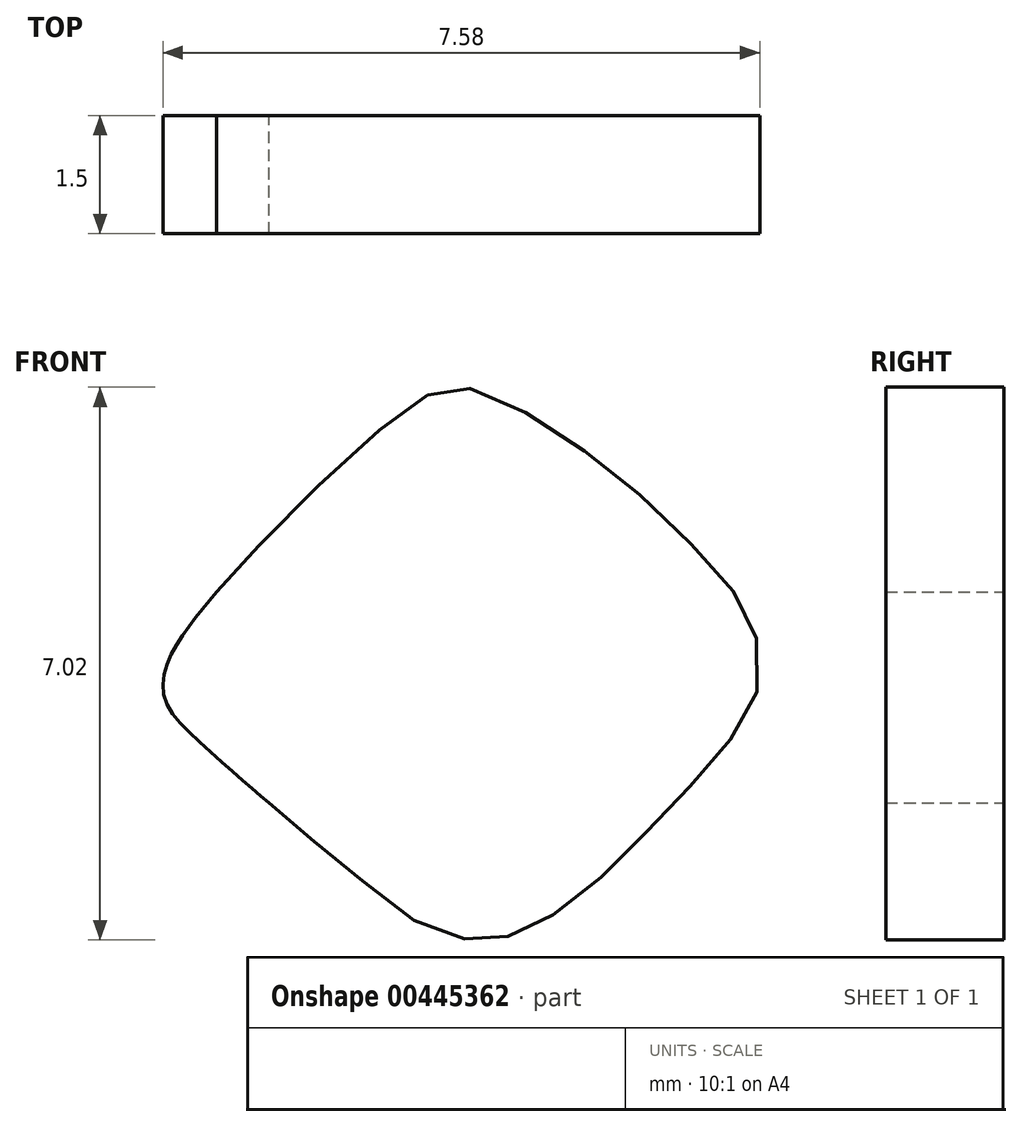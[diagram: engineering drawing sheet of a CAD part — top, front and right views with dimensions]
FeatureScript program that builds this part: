
annotation { "Feature Type Name" : "Feature", "Feature Type Description" : "" }
export const myFeature = defineFeature(function(context is Context, id is Id, definition is map)
    precondition{}
    {
        {
            var Q0;
            Q0=qCreatedBy(makeId("Front.planeOp"),FACE);
            var sketch = newSketch(context, id + "F0", { "sketchPlane" : qUnion([Q0])});
            skFitSpline(sketch, "E0", {"points": [v(-26.18, 6.87) * mm, v(-25.6, 7.51) * mm, v(-24.5, 8.6) * mm, v(-23.67, 9.27) * mm, v(-23.28, 9.45) * mm, v(-22.84, 9.42) * mm, v(-22.04, 9.02) * mm, v(-21.18, 8.41) * mm, v(-20.39, 7.72) * mm, v(-19.71, 7) * mm, v(-19.4, 6.52) * mm, v(-19.28, 5.87) * mm, v(-19.42, 5.35) * mm, v(-19.85, 4.75) * mm, v(-20.42, 4.13) * mm, v(-21.02, 3.52) * mm, v(-21.64, 2.95) * mm, v(-22.21, 2.6) * mm, v(-22.6, 2.46) * mm, v(-23.04, 2.46) * mm, v(-23.6, 2.65) * mm, v(-24.3, 3.18) * mm, v(-24.95, 3.7) * mm, v(-25.51, 4.19) * mm, v(-26.09, 4.74) * mm, v(-26.72, 5.35) * mm], "startDerivative": vector(12.36, 14.01) * mm, "endDerivative": vector(-15.04, 14.19) * mm});
            skLineSegment(sketch, "E1", {"start": v(-25.51, 4.19) * mm, "end": v(-25.33, 4.37) * mm});
            skLineSegment(sketch, "E2", {"start": v(-25.51, 4.19) * mm, "end": v(-25.73, 3.99) * mm});
            skFitSpline(sketch, "E3", {"points": [v(-26.18, 6.87) * mm, v(-26.45, 6.53) * mm, v(-26.7, 6.16) * mm, v(-26.85, 5.8) * mm, v(-26.8, 5.43) * mm, v(-26.45, 5.02) * mm, v(-25.89, 4.5) * mm, v(-25.51, 4.19) * mm], "startDerivative": vector(-2.07, -2.4) * mm, "endDerivative": vector(2.43, -2.05) * mm});
            skSolve(sketch);
        }
        {
            var Q0;
            Q0=makeQuery(id+"F0.imprint","IMPRINT",FACE,{"disambiguationData":[TD([[makeQuery(id+"F0.imprint","IMPRINT",EDGE,{"derivedFrom":sQuery(id+"F0.wireOp",EDGE,"E0")}),-1.0]])]});
            extrude(context, id + "F1", {"entities" : qUnion([Q0]), "depth" : 1.5 * mm});
        }
    });
